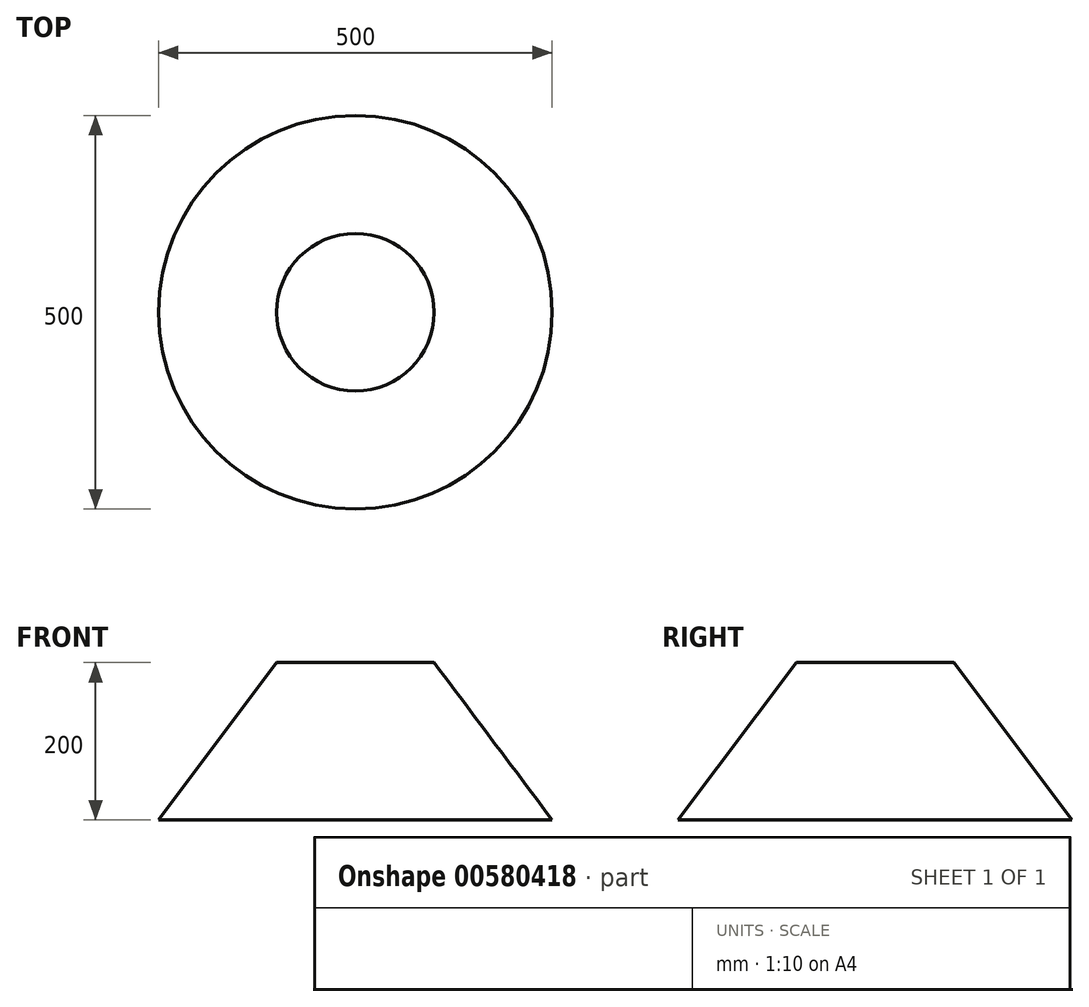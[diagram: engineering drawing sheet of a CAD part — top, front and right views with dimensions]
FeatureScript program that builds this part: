
annotation { "Feature Type Name" : "Feature", "Feature Type Description" : "" }
export const myFeature = defineFeature(function(context is Context, id is Id, definition is map)
    precondition{}
    {
        {
            var Q0;
            Q0=qCreatedBy(makeId("Top.planeOp"),FACE);
            var sketch = newSketch(context, id + "F0", { "sketchPlane" : qUnion([Q0])});
            skCircle(sketch, "E0", {"center": v(0, 0) * mm, "radius": 100 * mm});
            skSolve(sketch);
        }
        {
            var Q0;
            Q0=qCreatedBy(makeId("Top.planeOp"),FACE);
            cPlane(context, id + "F1", {"entities" : qUnion([Q0]), "cplaneType" : CPlaneType.OFFSET, "offset" : 200 * mm, "oppositeDirection" : true, "width" : 150 * mm, "height" : 150 * mm});
        }
        {
            var Q0;
            Q0=qCreatedBy(id+"F1.planeOp",FACE);
            var sketch = newSketch(context, id + "F2", { "sketchPlane" : qUnion([Q0])});
            skCircle(sketch, "E1", {"center": v(0, 0) * mm, "radius": 250 * mm});
            skSolve(sketch);
        }
        {
            var Q0;
            Q0=makeQuery(id+"F0.imprint","IMPRINT",FACE,{"disambiguationData":[TD([[makeQuery(id+"F0.imprint","IMPRINT",EDGE,{"derivedFrom":sQuery(id+"F0.wireOp",EDGE,"E0")}),1.0]])]});
            var Q1;
            Q1=makeQuery(id+"F2.imprint","IMPRINT",FACE,{"disambiguationData":[TD([[makeQuery(id+"F2.imprint","IMPRINT",EDGE,{"derivedFrom":sQuery(id+"F2.wireOp",EDGE,"E1")}),1.0]])]});
            loft(context, id + "F3", {"sheetProfilesArray" : [{ "sheetProfileEntities" : qUnion([Q0]) }, { "sheetProfileEntities" : qUnion([Q1]) }]});
        }
    });
